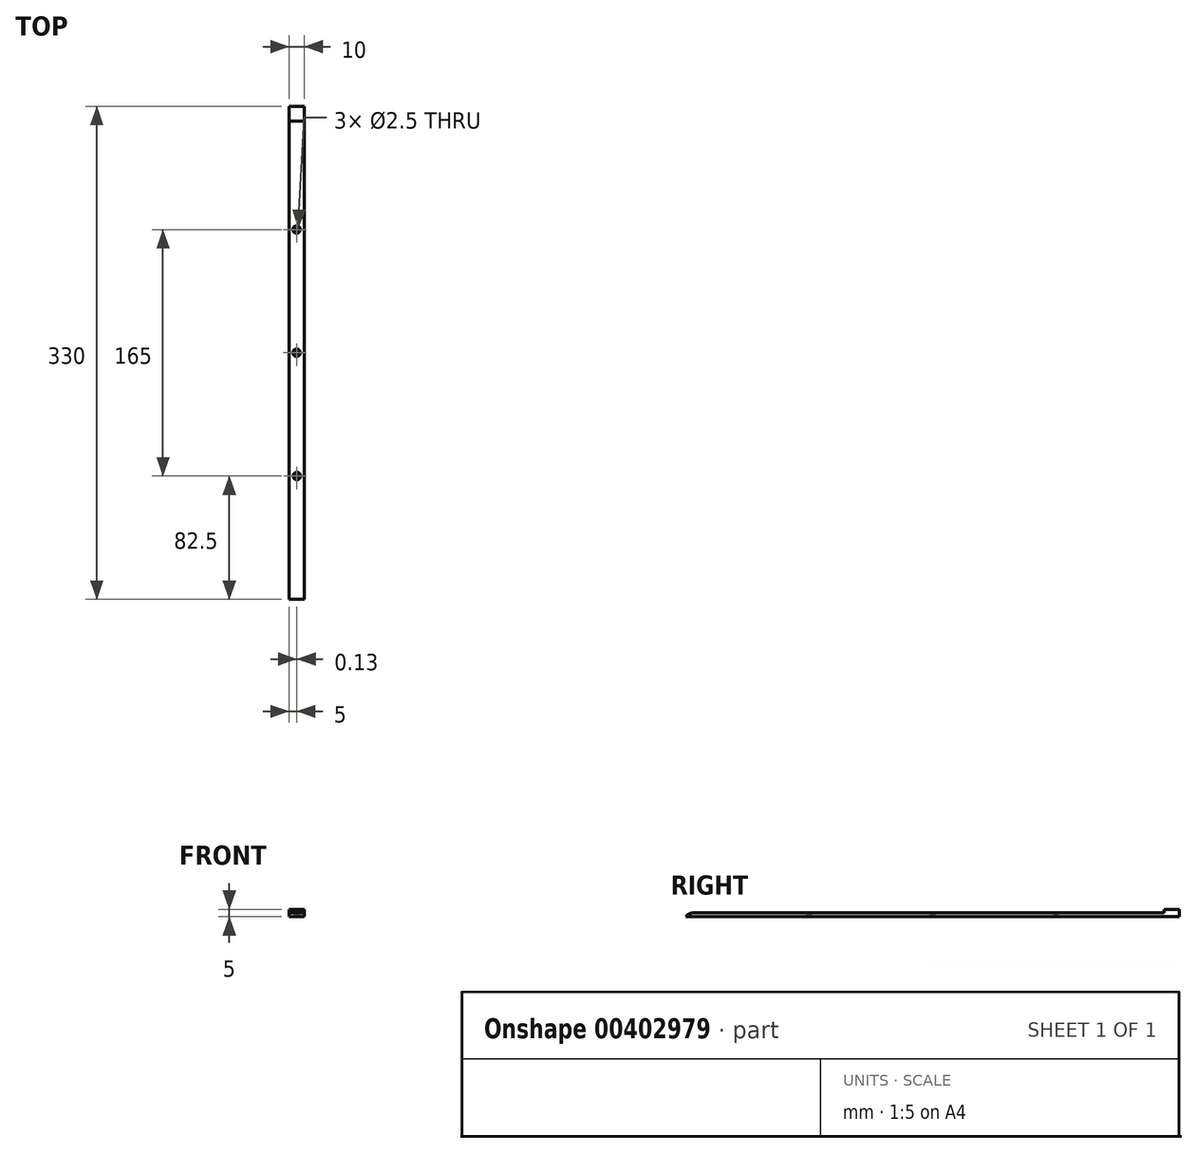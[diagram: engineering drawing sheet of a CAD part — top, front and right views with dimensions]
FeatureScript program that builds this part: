
annotation { "Feature Type Name" : "Feature", "Feature Type Description" : "" }
export const myFeature = defineFeature(function(context is Context, id is Id, definition is map)
    precondition{}
    {
        {
            var Q0;
            Q0=qCreatedBy(makeId("Top.planeOp"),FACE);
            var sketch = newSketch(context, id + "F0", { "sketchPlane" : qUnion([Q0])});
            skLineSegment(sketch, "E0.bottom", {"start": v(-5, 165) * mm, "end": v(5, 165) * mm});
            skLineSegment(sketch, "E0.top", {"start": v(-5, -165) * mm, "end": v(5, -165) * mm});
            skLineSegment(sketch, "E0.left", {"start": v(-5, 165) * mm, "end": v(-5, -165) * mm});
            skLineSegment(sketch, "E0.right", {"start": v(5, 165) * mm, "end": v(5, -165) * mm});
            skPoint(sketch, "E0.middle", {"position": v(0, 0) * mm});
            skLineSegment(sketch, "E1", {"start": v(-5, 155) * mm, "end": v(5, 155) * mm});
            skSolve(sketch);
        }
        {
            var Q0;
            {var subQ0=sQuery(id+"F0.wireOp",EDGE,"E0.top");Q0=makeQuery(id+"F0.imprint","IMPRINT",FACE,{"disambiguationData":[TD([[makeQuery(id+"F0.imprint","IMPRINT",EDGE,{"derivedFrom":subQ0}),1.0]])]});}
            extrude(context, id + "F1", {"entities" : qUnion([Q0]), "depth" : 2.5 * mm});
        }
        {
            var Q0;
            {var subQ0=sQuery(id+"F0.wireOp",EDGE,"E0.bottom");Q0=makeQuery(id+"F0.imprint","IMPRINT",FACE,{"disambiguationData":[TD([[makeQuery(id+"F0.imprint","IMPRINT",EDGE,{"derivedFrom":subQ0}),-1.0]])]});}
            extrude(context, id + "F2", {"entities" : qUnion([Q0]), "operationType" : NewBodyOperationType.ADD, "depth" : 5 * mm});
        }
        {
            var Q0;
            Q0=makeQuery(id+"F1.opExtrude","CAP_EDGE",EDGE,{"disambiguationData":[OSD([sQuery(id+"F0.wireOp",EDGE,"E0.top")])],"isStart":false});
            fillet(context, id + "F3", {"entities" : qUnion([Q0]), "radius" : 5 * mm, "tangentPropagation" : true, "allowEdgeOverflow" : false});
        }
        {
            var Q0;
            Q0=makeQuery(id+"F1.opExtrude","CAP_FACE",FACE,{"disambiguationData":[OSD([sQuery(id+"F0.wireOp",EDGE,"E0.top"),sQuery(id+"F0.wireOp",EDGE,"E0.left"),sQuery(id+"F0.wireOp",EDGE,"E0.right"),sQuery(id+"F0.wireOp",EDGE,"E1")])],"isStart":false});
            var sketch = newSketch(context, id + "F4", { "sketchPlane" : qUnion([Q0])});
            skPoint(sketch, "E2", {"position": v(0, 82.5) * mm});
            skPoint(sketch, "E3", {"position": v(0, 0) * mm});
            skPoint(sketch, "E4", {"position": v(0.13, -82.5) * mm});
            skSolve(sketch);
        }
        {
            var Q0;
            Q0=sQuery(id+"F4.wireOp",VERTEX,"E2");
            var Q1;
            Q1=sQuery(id+"F4.wireOp",VERTEX,"E3");
            var Q2;
            Q2=sQuery(id+"F4.wireOp",VERTEX,"E4");
            var Q3;
            Q3=makeQuery(id+"F1.opExtrude","SWEPT_BODY",BODY,{"disambiguationData":[OSD([sQuery(id+"F0.wireOp",EDGE,"E0.top"),sQuery(id+"F0.wireOp",EDGE,"E0.left"),sQuery(id+"F0.wireOp",EDGE,"E0.right"),sQuery(id+"F0.wireOp",EDGE,"E1")])]});
            hole(context, id + "F5", {"style" : HoleStyle.C_SINK, "endStyle" : HoleEndStyle.BLIND, "holeDiameter" : 2.5 * mm, "cSinkDiameter" : 5 * mm, "cSinkAngle" : 90 * degree, "holeDepth" : 2.5 * mm, "isTappedThrough" : true, "tappedDepth" : 12 * mm, "tapClearance" : 3, "startFromSketch" : true, "locations" : qUnion([Q0, Q1, Q2]), "scope" : qUnion([Q3])});
        }
    });
